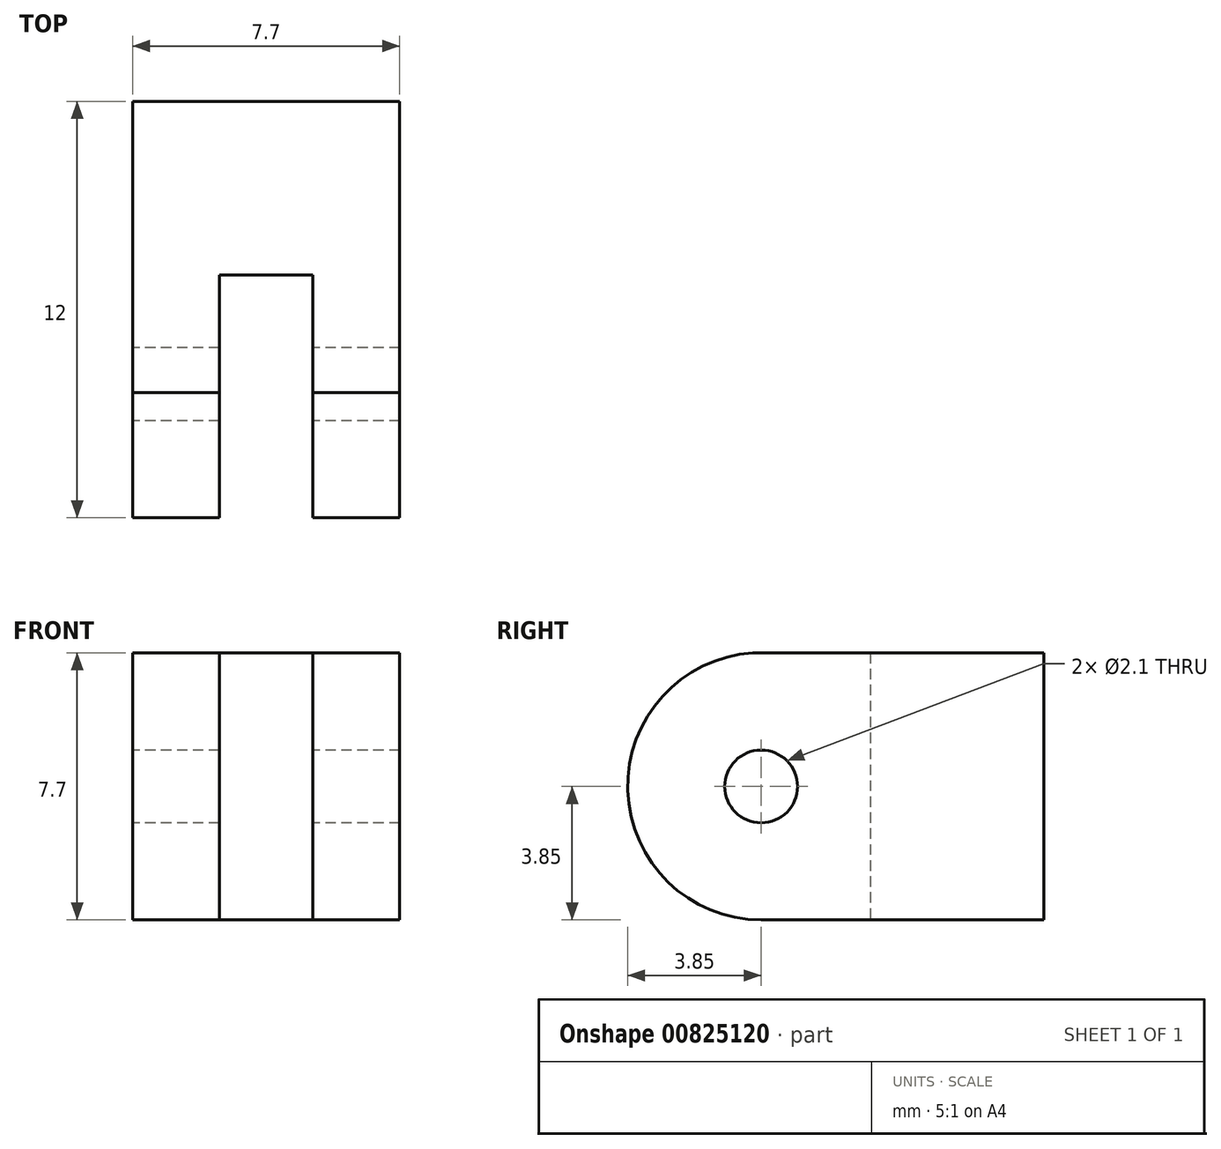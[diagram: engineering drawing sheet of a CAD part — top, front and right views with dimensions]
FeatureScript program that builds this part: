
annotation { "Feature Type Name" : "Feature", "Feature Type Description" : "" }
export const myFeature = defineFeature(function(context is Context, id is Id, definition is map)
    precondition{}
    {
        {
            var Q0;
            Q0=qCreatedBy(makeId("Top.planeOp"),FACE);
            var sketch = newSketch(context, id + "F0", { "sketchPlane" : qUnion([Q0])});
            skLineSegment(sketch, "E0", {"start": v(0, 31.32) * mm, "end": v(0, -51.9) * mm, "construction": true});
            skLineSegment(sketch, "E1", {"start": v(0, 0) * mm, "end": v(3.85, 0) * mm});
            skLineSegment(sketch, "E2", {"start": v(3.85, 0) * mm, "end": v(3.85, -12) * mm});
            skLineSegment(sketch, "E3", {"start": v(3.85, -12) * mm, "end": v(1.35, -12) * mm});
            skLineSegment(sketch, "E4", {"start": v(1.35, -12) * mm, "end": v(1.35, -5) * mm});
            skLineSegment(sketch, "E5", {"start": v(1.35, -5) * mm, "end": v(0, -5) * mm});
            skLineSegment(sketch, "E6.MirrorCS", {"start": v(0, 0) * mm, "end": v(-3.85, 0) * mm});
            skLineSegment(sketch, "E7.MirrorCS", {"start": v(-3.85, 0) * mm, "end": v(-3.85, -12) * mm});
            skLineSegment(sketch, "E8.MirrorCS", {"start": v(-3.85, -12) * mm, "end": v(-1.35, -12) * mm});
            skLineSegment(sketch, "E9.MirrorCS", {"start": v(-1.35, -12) * mm, "end": v(-1.35, -5) * mm});
            skLineSegment(sketch, "E10.MirrorCS", {"start": v(-1.35, -5) * mm, "end": v(0, -5) * mm});
            skSolve(sketch);
        }
        {
            var Q0;
            Q0 = qSketchRegion(id + "F0", true);
            extrude(context, id + "F1", {"entities" : qUnion([Q0]), "depth" : 7.7 * mm, "offsetDistance" : 25 * mm});
        }
        {
            var Q0;
            Q0=makeQuery(id+"F1.opExtrude","SWEPT_FACE",FACE,{"disambiguationData":[OSD([sQuery(id+"F0.wireOp",EDGE,"E7.MirrorCS")])]});
            var sketch = newSketch(context, id + "F2", { "sketchPlane" : qUnion([Q0])});
            skLineSegment(sketch, "E11", {"start": v(12, 3.85) * mm, "end": v(8.15, 3.85) * mm, "construction": true});
            skLineSegment(sketch, "E12", {"start": v(8.15, 7.7) * mm, "end": v(8.15, 0) * mm, "construction": true});
            skPoint(sketch, "E13", {"position": v(8.15, 3.85) * mm});
            skArc(sketch, "E14", {"start": v(8.15, 0) * mm, "mid": v(12, 3.85) * mm, "end": v(8.15, 7.7) * mm});
            skCircle(sketch, "E15", {"center": v(8.15, 3.85) * mm, "radius": 1.05 * mm});
            skSolve(sketch);
        }
        {
            var Q0;
            Q0=makeQuery(id+"F2.imprint","IMPRINT",FACE,{"disambiguationData":[TD([[makeQuery(id+"F2.imprint","IMPRINT",EDGE,{"derivedFrom":sQuery(id+"F2.wireOp",EDGE,"E15")}),1.0]])]});
            var Q1;
            {var subQ0=sQuery(id+"F2.wireOp",EDGE,"E14");var subQ1=sQuery(id+"F0.wireOp",EDGE,"E7.MirrorCS");var subQ2=makeQuery(id+"F1.opExtrude","CAP_EDGE",EDGE,{"disambiguationData":[OSD([subQ1])],"isStart":false});var subQ3=makeQuery(id+"F2.imprint","INTERSECT",VERTEX,{"derivedFrom":[subQ2,subQ0]});Q1=makeQuery(id+"F2.imprint","IMPRINT",FACE,{"disambiguationData":[TD([[makeQuery(id+"F2.imprint","IMPRINT",EDGE,{"disambiguationData":[TD([[subQ3,1.0]])],"derivedFrom":subQ0}),-1.0]])]});}
            var Q2;
            {var subQ0=sQuery(id+"F2.wireOp",EDGE,"E14");var subQ1=sQuery(id+"F0.wireOp",EDGE,"E7.MirrorCS");var subQ2=makeQuery(id+"F1.opExtrude","CAP_EDGE",EDGE,{"disambiguationData":[OSD([subQ1])],"isStart":true});var subQ3=makeQuery(id+"F2.imprint","INTERSECT",VERTEX,{"derivedFrom":[subQ2,subQ0]});Q2=makeQuery(id+"F2.imprint","IMPRINT",FACE,{"disambiguationData":[TD([[makeQuery(id+"F2.imprint","IMPRINT",EDGE,{"disambiguationData":[TD([[subQ3,-1.0]])],"derivedFrom":subQ0}),-1.0]])]});}
            extrude(context, id + "F3", {"entities" : qUnion([Q0, Q1, Q2]), "operationType" : NewBodyOperationType.REMOVE, "oppositeDirection" : true, "depth" : 10 * mm, "offsetDistance" : 25 * mm});
        }
    });
